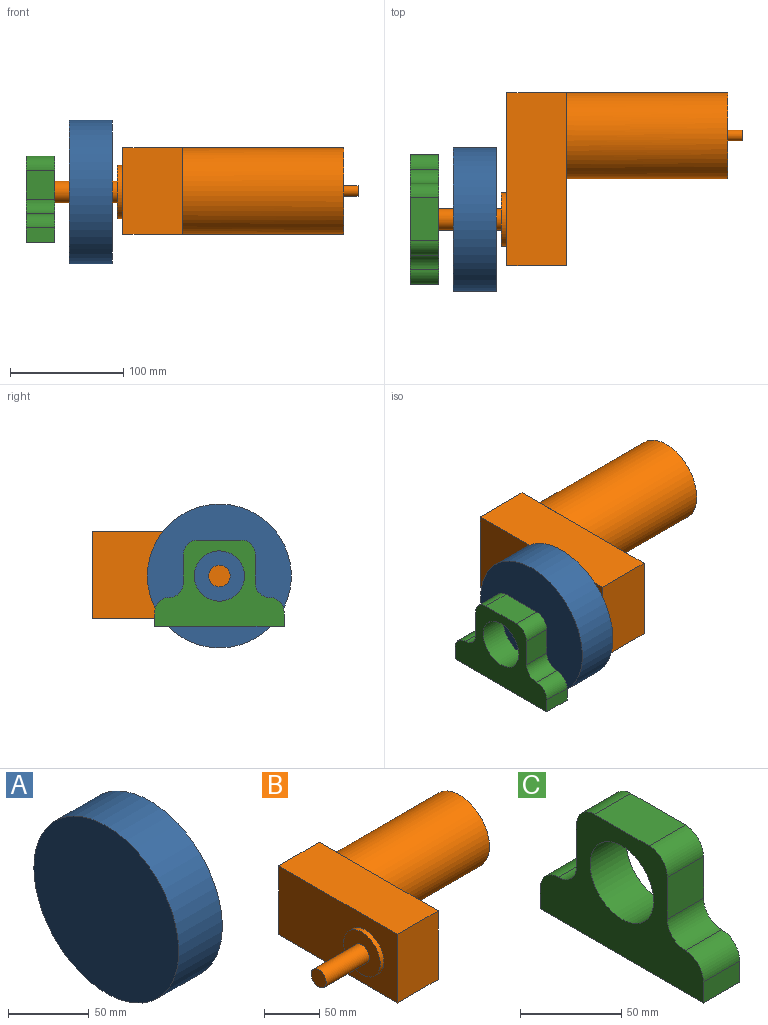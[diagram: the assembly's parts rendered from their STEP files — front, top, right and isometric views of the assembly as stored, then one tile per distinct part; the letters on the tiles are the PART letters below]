
ASSEMBLY  parts=3 mates=2
PART A: 3 faces, bbox 38.1x127x127 mm
  f0: cylinder r=63.5mm len=127mm, axis (-1,0,0), area 15201.2mm2, adj f1,f2
  f1: plane 127x127mm, normal (1,0,0), area 12667.7mm2, adj f0
  f2: plane 127x127mm, normal (-1,0,0), area 12667.7mm2, adj f0
PART B: 16 faces, bbox 267.7x152.4x76.2 mm
  f0: plane 37.59x31.9mm, normal (1,0,0), area 294.3mm2, adj f2,f6,f8
  f1: plane 114.81x76.2mm, normal (1,0,0), area 6468.2mm2, adj f4,f6,f7,f8
  f2: plane 194.82x76.2mm, normal (0,1,0), area 5754.3mm2, adj f0,f3,f5,f6,f7,f8,f9
  f3: plane 152.4x76.2mm, normal (-1,0,0), area 9878.7mm2, adj f2,f4,f6,f7,f10
  f4: plane 76.2x52.32mm, normal (0,-1,0), area 3987.1mm2, adj f1,f3,f6,f7
  f5: plane 37.59x31.9mm, normal (1,0,0), area 294.3mm2, adj f2,f7,f8
  f6: plane 152.4x52.32mm, normal (0,0,1), area 7974.2mm2, adj f0,f1,f2,f3,f4
  f7: plane 152.4x52.32mm, normal (0,0,-1), area 7974.2mm2, adj f1,f2,f3,f4,f5
  f8: cylinder r=38.1mm len=142.49mm, axis (-1,0,0), area 32336.5mm2, adj f0,f1,f2,f5,f9
  f9: plane 76.2x75.69mm, normal (1,0,0), area 4484.9mm2, adj f2,f8,f14
  f10: cylinder r=23.49mm len=46.99mm, axis (1,0,0), area 712.4mm2, adj f3,f11
  f11: plane 46.99x46.99mm, normal (-1,0,0), area 1449.2mm2, adj f10,f12
  f12: cylinder r=9.53mm len=55.37mm, axis (1,0,0), area 3313.9mm2, adj f11,f13
  f13: plane 19.05x19.05mm, normal (-1,0,0), area 285mm2, adj f12
  f14: cylinder r=4.76mm len=12.7mm, axis (-1,0,0), area 380mm2, adj f9,f15
  f15: plane 9.53x9.53mm, normal (1,0,0), area 71.3mm2, adj f14
PART C: 15 faces, bbox 25.4x114.3x76.2 mm
  f0: plane 25.4x25.4mm, normal (0,-1,0), area 645.2mm2, adj f4,f5,f10,f13
  f1: plane 38.1x25.4mm, normal (0,0,1), area 967.7mm2, adj f4,f5,f13,f14
  f2: plane 114.3x25.4mm, normal (0,0,-1), area 2903.2mm2, adj f4,f5,f7,f8
  f3: plane 25.4x25.4mm, normal (0,1,0), area 645.2mm2, adj f4,f5,f12,f14
  f4: plane 114.3x76.2mm, normal (1,0,0), area 4508mm2, adj f0,f1,f2,f3,f6,f7,f8,f9
  f5: plane 114.3x76.2mm, normal (-1,0,0), area 4508mm2, adj f0,f1,f2,f3,f6,f7,f8,f9
  f6: cylinder r=22.23mm len=44.45mm, axis (1,0,0), area 3547mm2, adj f4,f5
  f7: plane 25.4x12.7mm, normal (0,1,0), area 322.6mm2, adj f2,f4,f5,f11
  f8: plane 25.4x12.7mm, normal (0,-1,0), area 322.6mm2, adj f2,f4,f5,f9
  f9: cylinder r=12.7mm len=25.4mm, axis (1,0,0), area 506.7mm2, adj f4,f5,f8,f10
  f10: cylinder r=12.7mm len=25.4mm, axis (-1,0,0), area 506.7mm2, adj f0,f4,f5,f9
  f11: cylinder r=12.7mm len=25.4mm, axis (-1,0,0), area 506.7mm2, adj f4,f5,f7,f12
  f12: cylinder r=12.7mm len=25.4mm, axis (-1,0,0), area 506.7mm2, adj f3,f4,f5,f11
  f13: cylinder r=12.7mm len=25.4mm, axis (-1,0,0), area 506.7mm2, adj f0,f1,f4,f5
  f14: cylinder r=12.7mm len=25.4mm, axis (1,0,0), area 506.7mm2, adj f1,f3,f4,f5
PLACE A t=(-181.12,126.29,-184.51)mm
PLACE B t=(-133.62,85.59,-221.66)mm
PLACE C t=(-219.22,292.58,-203.61)mm
MATE revolute B.f10 <-> A.f0  axis (-1,0,0) through (-193.82,126.29,-184.51)mm
MATE revolute B.f10 <-> C.f6  axis (-1,0,0) through (-193.82,126.29,-184.51)mm
